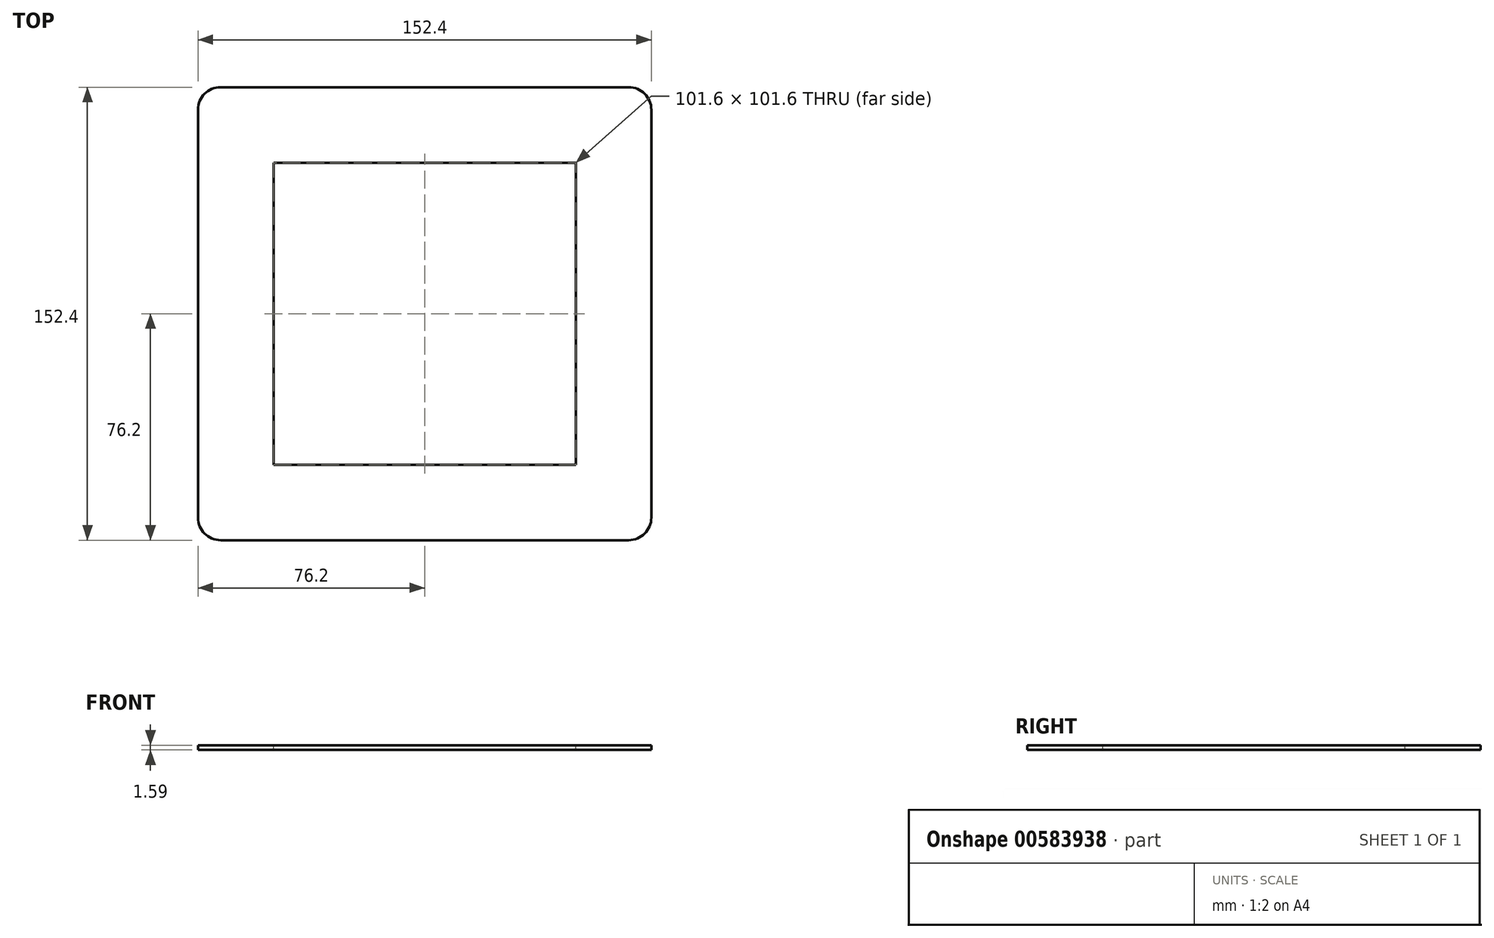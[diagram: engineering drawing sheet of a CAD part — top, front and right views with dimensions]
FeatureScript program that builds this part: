
annotation { "Feature Type Name" : "Feature", "Feature Type Description" : "" }
export const myFeature = defineFeature(function(context is Context, id is Id, definition is map)
    precondition{}
    {
        {
            var Q0;
            Q0=qCreatedBy(makeId("Top.planeOp"),FACE);
            var sketch = newSketch(context, id + "F0", { "sketchPlane" : qUnion([Q0])});
            skLineSegment(sketch, "E0.bottom", {"start": v(76.2, 76.2) * mm, "end": v(-76.2, 76.2) * mm});
            skLineSegment(sketch, "E0.top", {"start": v(76.2, -76.2) * mm, "end": v(-76.2, -76.2) * mm});
            skLineSegment(sketch, "E0.left", {"start": v(76.2, 76.2) * mm, "end": v(76.2, -76.2) * mm});
            skLineSegment(sketch, "E0.right", {"start": v(-76.2, 76.2) * mm, "end": v(-76.2, -76.2) * mm});
            skPoint(sketch, "E0.middle", {"position": v(0, 0) * mm});
            skSolve(sketch);
        }
        {
            var Q0;
            Q0=makeQuery(id+"F0.imprint","IMPRINT",FACE,{"disambiguationData":[TD([[makeQuery(id+"F0.imprint","IMPRINT",EDGE,{"derivedFrom":sQuery(id+"F0.wireOp",EDGE,"E0.bottom")}),1.0]])]});
            extrude(context, id + "F1", {"entities" : qUnion([Q0]), "depth" : 1.59 * mm, "offsetDistance" : 25.4 * mm});
        }
        {
            var Q0;
            Q0=makeQuery(id+"F1.opExtrude","SWEPT_EDGE",EDGE,{"disambiguationData":[OSD([sQuery(id+"F0.wireOp",EDGE,"E0.bottom"),sQuery(id+"F0.wireOp",EDGE,"E0.left")])]});
            var Q1;
            Q1=makeQuery(id+"F1.opExtrude","SWEPT_EDGE",EDGE,{"disambiguationData":[OSD([sQuery(id+"F0.wireOp",EDGE,"E0.top"),sQuery(id+"F0.wireOp",EDGE,"E0.right")])]});
            var Q2;
            Q2=makeQuery(id+"F1.opExtrude","SWEPT_EDGE",EDGE,{"disambiguationData":[OSD([sQuery(id+"F0.wireOp",EDGE,"E0.top"),sQuery(id+"F0.wireOp",EDGE,"E0.left")])]});
            var Q3;
            Q3=makeQuery(id+"F1.opExtrude","SWEPT_EDGE",EDGE,{"disambiguationData":[OSD([sQuery(id+"F0.wireOp",EDGE,"E0.bottom"),sQuery(id+"F0.wireOp",EDGE,"E0.right")])]});
            fillet(context, id + "F2", {"entities" : qUnion([Q0, Q1, Q2, Q3]), "radius" : 7.62 * mm, "tangentPropagation" : true, "allowEdgeOverflow" : false});
        }
        {
            var Q0;
            Q0=makeQuery(id+"F1.opExtrude","CAP_FACE",FACE,{"disambiguationData":[OSD([sQuery(id+"F0.wireOp",EDGE,"E0.bottom"),sQuery(id+"F0.wireOp",EDGE,"E0.top"),sQuery(id+"F0.wireOp",EDGE,"E0.left"),sQuery(id+"F0.wireOp",EDGE,"E0.right")])],"isStart":false});
            var sketch = newSketch(context, id + "F3", { "sketchPlane" : qUnion([Q0])});
            skLineSegment(sketch, "E1.bottom", {"start": v(50.8, 50.8) * mm, "end": v(-50.8, 50.8) * mm});
            skLineSegment(sketch, "E1.top", {"start": v(50.8, -50.8) * mm, "end": v(-50.8, -50.8) * mm});
            skLineSegment(sketch, "E1.left", {"start": v(50.8, 50.8) * mm, "end": v(50.8, -50.8) * mm});
            skLineSegment(sketch, "E1.right", {"start": v(-50.8, 50.8) * mm, "end": v(-50.8, -50.8) * mm});
            skPoint(sketch, "E1.middle", {"position": v(0, 0) * mm});
            skSolve(sketch);
        }
        {
            var Q0;
            Q0 = qSketchRegion(id + "F3", true);
            extrude(context, id + "F4", {"entities" : qUnion([Q0]), "operationType" : NewBodyOperationType.REMOVE, "endBound" : BoundingType.THROUGH_ALL, "oppositeDirection" : true, "depth" : 25.4 * mm, "offsetDistance" : 25.4 * mm});
        }
    });
